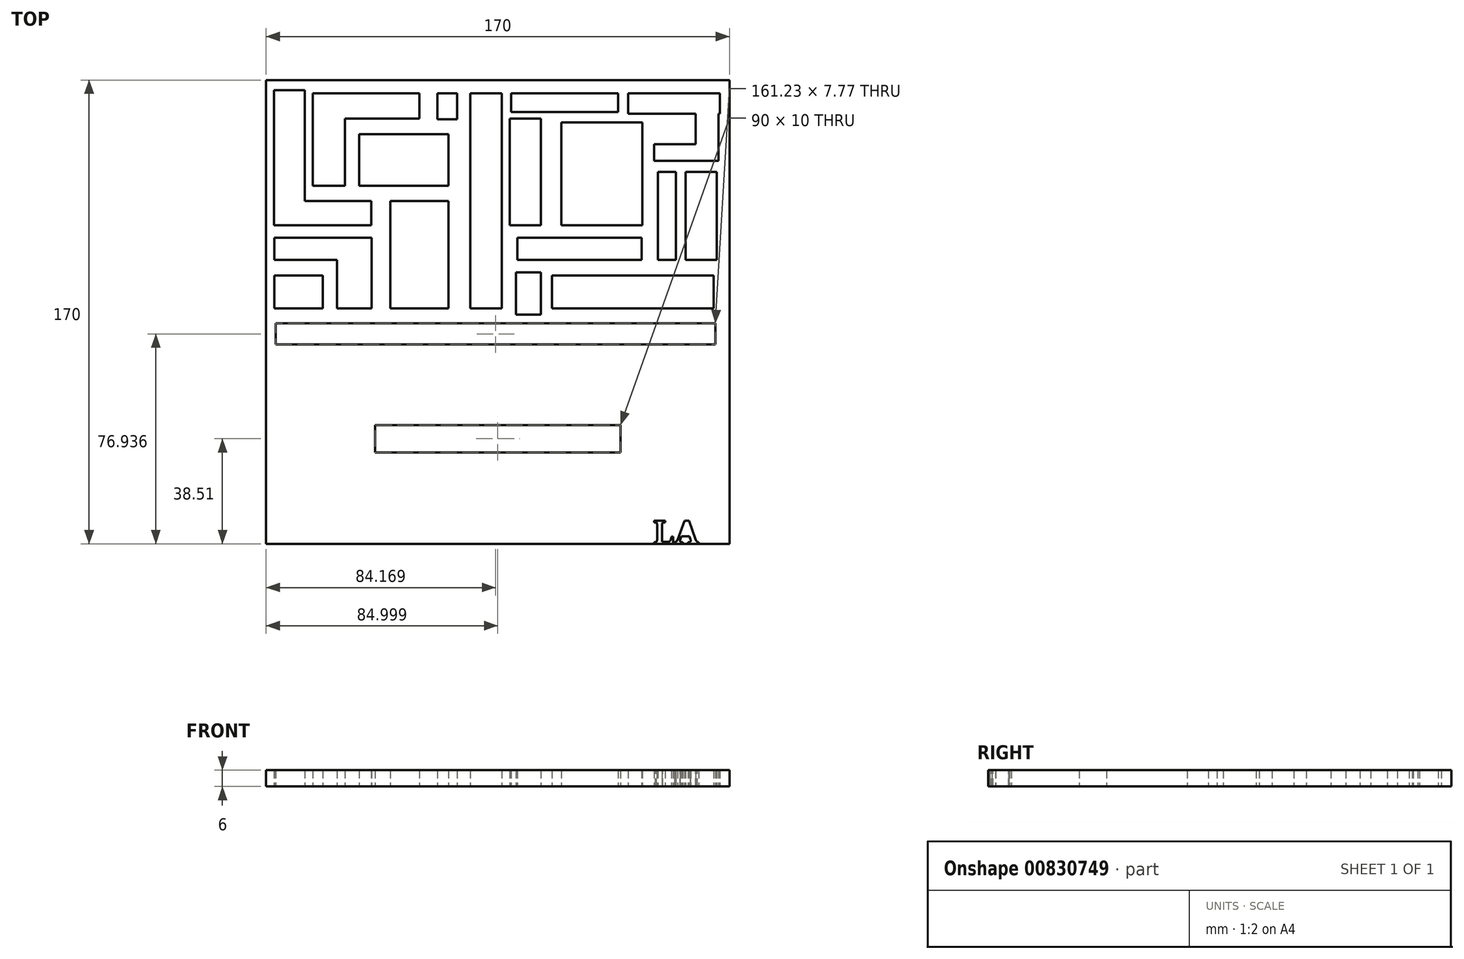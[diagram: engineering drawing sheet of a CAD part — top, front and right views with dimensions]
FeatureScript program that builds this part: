
annotation { "Feature Type Name" : "Feature", "Feature Type Description" : "" }
export const myFeature = defineFeature(function(context is Context, id is Id, definition is map)
    precondition{}
    {
        {
            var Q0;
            Q0=qCreatedBy(makeId("Top.planeOp"),FACE);
            var sketch = newSketch(context, id + "F0", { "sketchPlane" : qUnion([Q0])});
            skLineSegment(sketch, "E0.bottom", {"start": v(-132.8, 144.42) * mm, "end": v(37.2, 144.42) * mm});
            skLineSegment(sketch, "E0.top", {"start": v(-132.8, -25.58) * mm, "end": v(37.2, -25.58) * mm});
            skLineSegment(sketch, "E0.left", {"start": v(-132.8, 144.42) * mm, "end": v(-132.8, -25.58) * mm});
            skLineSegment(sketch, "E0.right", {"start": v(37.2, 144.42) * mm, "end": v(37.2, -25.58) * mm});
            skLineSegment(sketch, "E1.bottom", {"start": v(-92.8, 17.93) * mm, "end": v(-2.8, 17.93) * mm});
            skLineSegment(sketch, "E1.top", {"start": v(-92.8, 7.93) * mm, "end": v(-2.8, 7.93) * mm});
            skLineSegment(sketch, "E1.left", {"start": v(-92.8, 17.93) * mm, "end": v(-92.8, 7.93) * mm});
            skLineSegment(sketch, "E1.right", {"start": v(-2.8, 17.93) * mm, "end": v(-2.8, 7.93) * mm});
            skText(sketch, "E2", { "text": "LA", "fontName": "NotoSerif-Bold.ttf"});
            skLineSegment(sketch, "E3.bottom", {"start": v(-129.9, 140.75) * mm, "end": v(-118.66, 140.75) * mm});
            skLineSegment(sketch, "E3.top", {"start": v(-129.9, 91.23) * mm, "end": v(-118.66, 91.23) * mm});
            skLineSegment(sketch, "E3.left", {"start": v(-129.9, 140.75) * mm, "end": v(-129.9, 91.23) * mm});
            skLineSegment(sketch, "E3.right", {"start": v(-118.66, 140.75) * mm, "end": v(-118.66, 91.23) * mm});
            skLineSegment(sketch, "E4.bottom", {"start": v(-118.66, 100.16) * mm, "end": v(-94.2, 100.16) * mm});
            skLineSegment(sketch, "E4.top", {"start": v(-118.66, 91.23) * mm, "end": v(-94.2, 91.23) * mm});
            skLineSegment(sketch, "E4.left", {"start": v(-118.66, 100.16) * mm, "end": v(-118.66, 91.23) * mm});
            skLineSegment(sketch, "E4.right", {"start": v(-94.2, 100.16) * mm, "end": v(-94.2, 91.23) * mm});
            skLineSegment(sketch, "E5.bottom", {"start": v(-115.71, 105.63) * mm, "end": v(-103.9, 105.63) * mm});
            skLineSegment(sketch, "E5.top", {"start": v(-115.71, 139.6) * mm, "end": v(-103.9, 139.6) * mm});
            skLineSegment(sketch, "E5.left", {"start": v(-115.71, 105.63) * mm, "end": v(-115.71, 139.6) * mm});
            skLineSegment(sketch, "E5.right", {"start": v(-103.9, 105.63) * mm, "end": v(-103.9, 139.6) * mm});
            skLineSegment(sketch, "E6.bottom", {"start": v(-103.9, 139.6) * mm, "end": v(-76.56, 139.6) * mm});
            skLineSegment(sketch, "E6.top", {"start": v(-103.9, 130.39) * mm, "end": v(-76.56, 130.39) * mm});
            skLineSegment(sketch, "E6.left", {"start": v(-103.9, 139.6) * mm, "end": v(-103.9, 130.39) * mm});
            skLineSegment(sketch, "E6.right", {"start": v(-76.56, 139.6) * mm, "end": v(-76.56, 130.39) * mm});
            skLineSegment(sketch, "E7.bottom", {"start": v(-129.82, 86.62) * mm, "end": v(-94.12, 86.62) * mm});
            skLineSegment(sketch, "E7.top", {"start": v(-129.82, 78.56) * mm, "end": v(-94.12, 78.56) * mm});
            skLineSegment(sketch, "E7.left", {"start": v(-129.82, 86.62) * mm, "end": v(-129.82, 78.56) * mm});
            skLineSegment(sketch, "E7.right", {"start": v(-94.12, 86.62) * mm, "end": v(-94.12, 78.56) * mm});
            skLineSegment(sketch, "E8.bottom", {"start": v(-106.79, 78.56) * mm, "end": v(-94.12, 78.56) * mm});
            skLineSegment(sketch, "E8.top", {"start": v(-106.79, 60.71) * mm, "end": v(-94.12, 60.71) * mm});
            skLineSegment(sketch, "E8.left", {"start": v(-106.79, 78.56) * mm, "end": v(-106.79, 60.71) * mm});
            skLineSegment(sketch, "E8.right", {"start": v(-94.12, 78.56) * mm, "end": v(-94.12, 60.71) * mm});
            skLineSegment(sketch, "E9.bottom", {"start": v(-129.82, 72.8) * mm, "end": v(-111.97, 72.8) * mm});
            skLineSegment(sketch, "E9.top", {"start": v(-129.82, 60.71) * mm, "end": v(-111.97, 60.71) * mm});
            skLineSegment(sketch, "E9.left", {"start": v(-129.82, 72.8) * mm, "end": v(-129.82, 60.71) * mm});
            skLineSegment(sketch, "E9.right", {"start": v(-111.97, 72.8) * mm, "end": v(-111.97, 60.71) * mm});
            skLineSegment(sketch, "E10.bottom", {"start": v(-98.73, 124.63) * mm, "end": v(-65.9, 124.63) * mm});
            skLineSegment(sketch, "E10.top", {"start": v(-98.73, 105.63) * mm, "end": v(-65.9, 105.63) * mm});
            skLineSegment(sketch, "E10.left", {"start": v(-98.73, 124.63) * mm, "end": v(-98.73, 105.63) * mm});
            skLineSegment(sketch, "E10.right", {"start": v(-65.9, 124.63) * mm, "end": v(-65.9, 105.63) * mm});
            skLineSegment(sketch, "E11.bottom", {"start": v(-87.2, 100.16) * mm, "end": v(-65.9, 100.16) * mm});
            skLineSegment(sketch, "E11.top", {"start": v(-87.2, 60.71) * mm, "end": v(-65.9, 60.71) * mm});
            skLineSegment(sketch, "E11.left", {"start": v(-87.2, 100.16) * mm, "end": v(-87.2, 60.71) * mm});
            skLineSegment(sketch, "E11.right", {"start": v(-65.9, 100.16) * mm, "end": v(-65.9, 60.71) * mm});
            skLineSegment(sketch, "E12.bottom", {"start": v(-69.94, 139.6) * mm, "end": v(-62.74, 139.6) * mm});
            skLineSegment(sketch, "E12.top", {"start": v(-69.94, 130.1) * mm, "end": v(-62.74, 130.1) * mm});
            skLineSegment(sketch, "E12.left", {"start": v(-69.94, 139.6) * mm, "end": v(-69.94, 130.1) * mm});
            skLineSegment(sketch, "E12.right", {"start": v(-62.74, 139.6) * mm, "end": v(-62.74, 130.1) * mm});
            skLineSegment(sketch, "E13.bottom", {"start": v(-57.84, 139.6) * mm, "end": v(-46.33, 139.6) * mm});
            skLineSegment(sketch, "E13.top", {"start": v(-57.84, 60.71) * mm, "end": v(-46.33, 60.71) * mm});
            skLineSegment(sketch, "E13.left", {"start": v(-57.84, 139.6) * mm, "end": v(-57.84, 60.71) * mm});
            skLineSegment(sketch, "E13.right", {"start": v(-46.33, 139.6) * mm, "end": v(-46.33, 60.71) * mm});
            skLineSegment(sketch, "E14.bottom", {"start": v(-42.87, 139.6) * mm, "end": v(-3.72, 139.6) * mm});
            skLineSegment(sketch, "E14.top", {"start": v(-42.87, 132.69) * mm, "end": v(-3.72, 132.69) * mm});
            skLineSegment(sketch, "E14.left", {"start": v(-42.87, 139.6) * mm, "end": v(-42.87, 132.69) * mm});
            skLineSegment(sketch, "E14.right", {"start": v(-3.72, 139.6) * mm, "end": v(-3.72, 132.69) * mm});
            skLineSegment(sketch, "E15.bottom", {"start": v(-43.45, 130.39) * mm, "end": v(-31.93, 130.39) * mm});
            skLineSegment(sketch, "E15.top", {"start": v(-43.45, 91.23) * mm, "end": v(-31.93, 91.23) * mm});
            skLineSegment(sketch, "E15.left", {"start": v(-43.45, 130.39) * mm, "end": v(-43.45, 91.23) * mm});
            skLineSegment(sketch, "E15.right", {"start": v(-31.93, 130.39) * mm, "end": v(-31.93, 91.23) * mm});
            skLineSegment(sketch, "E16.bottom", {"start": v(-24.45, 128.95) * mm, "end": v(5.2, 128.95) * mm});
            skLineSegment(sketch, "E16.top", {"start": v(-24.45, 91.23) * mm, "end": v(5.2, 91.23) * mm});
            skLineSegment(sketch, "E16.left", {"start": v(-24.45, 128.95) * mm, "end": v(-24.45, 91.23) * mm});
            skLineSegment(sketch, "E16.right", {"start": v(5.2, 128.95) * mm, "end": v(5.2, 91.23) * mm});
            skLineSegment(sketch, "E17.bottom", {"start": v(-40.57, 86.62) * mm, "end": v(4.92, 86.62) * mm});
            skLineSegment(sketch, "E17.top", {"start": v(-40.57, 78.56) * mm, "end": v(4.92, 78.56) * mm});
            skLineSegment(sketch, "E17.left", {"start": v(-40.57, 86.62) * mm, "end": v(-40.57, 78.56) * mm});
            skLineSegment(sketch, "E17.right", {"start": v(4.92, 86.62) * mm, "end": v(4.92, 78.56) * mm});
            skLineSegment(sketch, "E18.bottom", {"start": v(-41.15, 73.96) * mm, "end": v(-31.93, 73.96) * mm});
            skLineSegment(sketch, "E18.top", {"start": v(-41.15, 58.41) * mm, "end": v(-31.93, 58.41) * mm});
            skLineSegment(sketch, "E18.left", {"start": v(-41.15, 73.96) * mm, "end": v(-41.15, 58.41) * mm});
            skLineSegment(sketch, "E18.right", {"start": v(-31.93, 73.96) * mm, "end": v(-31.93, 58.41) * mm});
            skLineSegment(sketch, "E19.bottom", {"start": v(-27.9, 72.8) * mm, "end": v(31.4, 72.8) * mm});
            skLineSegment(sketch, "E19.top", {"start": v(-27.9, 60.71) * mm, "end": v(31.4, 60.71) * mm});
            skLineSegment(sketch, "E19.left", {"start": v(-27.9, 72.8) * mm, "end": v(-27.9, 60.71) * mm});
            skLineSegment(sketch, "E19.right", {"start": v(31.4, 72.8) * mm, "end": v(31.4, 60.71) * mm});
            skLineSegment(sketch, "E20.bottom", {"start": v(10.97, 78.56) * mm, "end": v(17.59, 78.56) * mm});
            skLineSegment(sketch, "E20.top", {"start": v(10.97, 110.8) * mm, "end": v(17.59, 110.8) * mm});
            skLineSegment(sketch, "E20.left", {"start": v(10.97, 78.56) * mm, "end": v(10.97, 110.8) * mm});
            skLineSegment(sketch, "E20.right", {"start": v(17.59, 78.56) * mm, "end": v(17.59, 110.8) * mm});
            skLineSegment(sketch, "E21.bottom", {"start": v(21.04, 110.8) * mm, "end": v(32.56, 110.8) * mm});
            skLineSegment(sketch, "E21.top", {"start": v(21.04, 78.56) * mm, "end": v(32.56, 78.56) * mm});
            skLineSegment(sketch, "E21.left", {"start": v(21.04, 110.8) * mm, "end": v(21.04, 78.56) * mm});
            skLineSegment(sketch, "E21.right", {"start": v(32.56, 110.8) * mm, "end": v(32.56, 78.56) * mm});
            skLineSegment(sketch, "E22.bottom", {"start": v(9.53, 114.84) * mm, "end": v(33.13, 114.84) * mm});
            skLineSegment(sketch, "E22.top", {"start": v(9.53, 120.89) * mm, "end": v(33.13, 120.89) * mm});
            skLineSegment(sketch, "E22.left", {"start": v(9.53, 114.84) * mm, "end": v(9.53, 120.89) * mm});
            skLineSegment(sketch, "E22.right", {"start": v(33.13, 114.84) * mm, "end": v(33.13, 120.89) * mm});
            skLineSegment(sketch, "E23.bottom", {"start": v(0, 139.6) * mm, "end": v(33.7, 139.6) * mm});
            skLineSegment(sketch, "E23.top", {"start": v(0, 132.11) * mm, "end": v(33.7, 132.11) * mm});
            skLineSegment(sketch, "E23.left", {"start": v(0, 139.6) * mm, "end": v(0, 132.11) * mm});
            skLineSegment(sketch, "E23.right", {"start": v(33.7, 139.6) * mm, "end": v(33.7, 132.11) * mm});
            skLineSegment(sketch, "E24.bottom", {"start": v(24.78, 132.11) * mm, "end": v(33.13, 132.11) * mm});
            skLineSegment(sketch, "E24.top", {"start": v(24.78, 120.89) * mm, "end": v(33.13, 120.89) * mm});
            skLineSegment(sketch, "E24.left", {"start": v(24.78, 132.11) * mm, "end": v(24.78, 120.89) * mm});
            skLineSegment(sketch, "E24.right", {"start": v(33.13, 132.11) * mm, "end": v(33.13, 120.89) * mm});
            skLineSegment(sketch, "E25.bottom", {"start": v(-129.24, 55.24) * mm, "end": v(31.98, 55.24) * mm});
            skLineSegment(sketch, "E25.top", {"start": v(-129.24, 47.47) * mm, "end": v(31.98, 47.47) * mm});
            skLineSegment(sketch, "E25.left", {"start": v(-129.24, 55.24) * mm, "end": v(-129.24, 47.47) * mm});
            skLineSegment(sketch, "E25.right", {"start": v(31.98, 55.24) * mm, "end": v(31.98, 47.47) * mm});
            const initialGuessF0  = {"E2": [0.00917, -0.02558, 1, 0, 0.00858]};
            skSetInitialGuess(sketch, initialGuessF0);
            skSolve(sketch);
        }
        {
            var Q0;
            Q0=makeQuery(id+"F0.imprint","IMPRINT",FACE,{"disambiguationData":[TD([[makeQuery(id+"F0.imprint","IMPRINT",EDGE,{"derivedFrom":sQuery(id+"F0.wireOp",EDGE,"E0.bottom")}),-1.0]])]});
            extrude(context, id + "F1", {"entities" : qUnion([Q0]), "depth" : 6 * mm, "offsetDistance" : 25 * mm});
        }
    });
